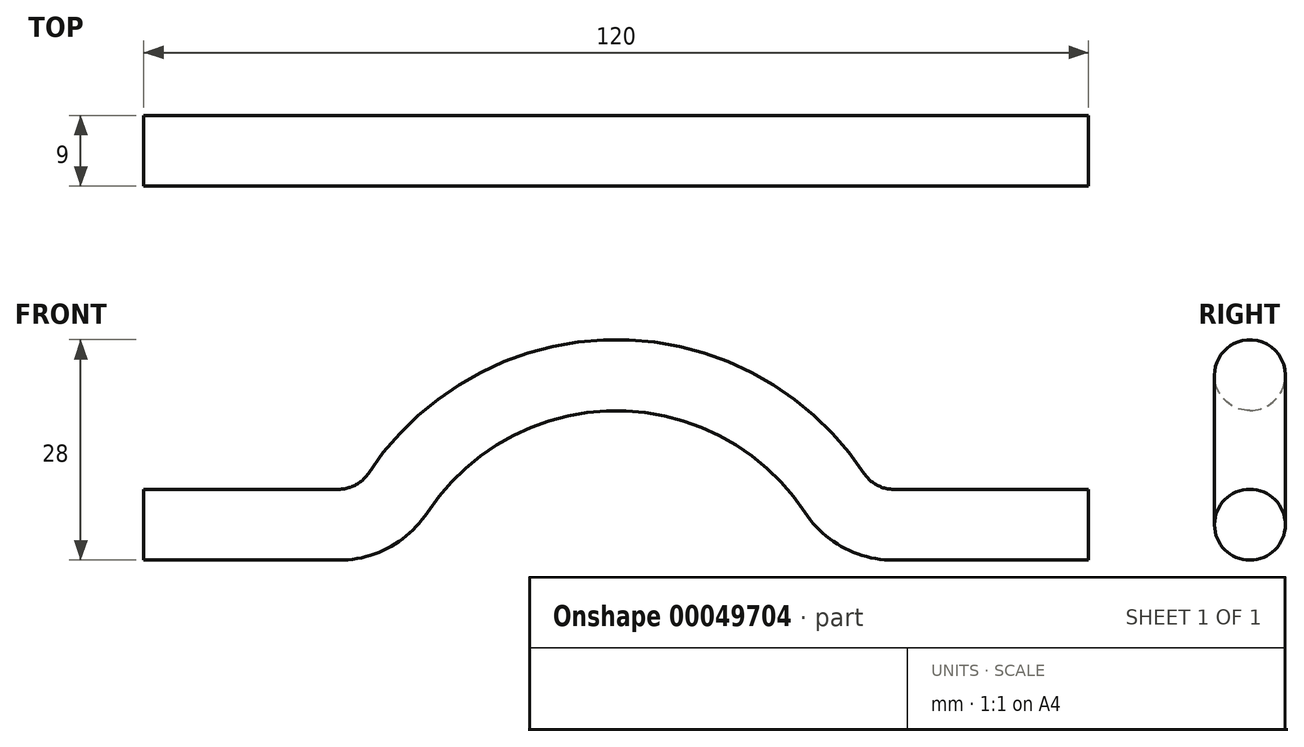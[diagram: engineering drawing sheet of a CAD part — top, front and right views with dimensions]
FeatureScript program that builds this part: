
annotation { "Feature Type Name" : "Feature", "Feature Type Description" : "" }
export const myFeature = defineFeature(function(context is Context, id is Id, definition is map)
    precondition{}
    {
        {
            var Q0;
            Q0=qCreatedBy(makeId("Front.planeOp"),FACE);
            var sketch = newSketch(context, id + "F0", { "sketchPlane" : qUnion([Q0])});
            skLineSegment(sketch, "E0", {"start": v(0, 0) * mm, "end": v(24.76, 0) * mm});
            skLineSegment(sketch, "E1", {"start": v(60, 23.82) * mm, "end": v(60, -14.96) * mm, "construction": true});
            skArc(sketch, "E2", {"start": v(60, 19) * mm, "mid": v(44.25, 15.03) * mm, "end": v(32.28, 4.05) * mm});
            skArc(sketch, "E3", {"start": v(87.72, 4.05) * mm, "mid": v(75.75, 15.03) * mm, "end": v(60, 19) * mm});
            skLineSegment(sketch, "E4", {"start": v(95.24, 0) * mm, "end": v(120, 0) * mm});
            skPoint(sketch, "E5.visualSharp", {"position": v(30, 0) * mm});
            skArc(sketch, "E5.filletArc", {"start": v(24.76, 0) * mm, "mid": v(29.03, 1.08) * mm, "end": v(32.28, 4.05) * mm});
            skPoint(sketch, "E6.visualSharp", {"position": v(90, 0) * mm});
            skArc(sketch, "E6.filletArc", {"start": v(87.72, 4.05) * mm, "mid": v(90.97, 1.08) * mm, "end": v(95.24, 0) * mm});
            skSolve(sketch);
        }
        {
            var Q0;
            Q0=qCreatedBy(makeId("Right.planeOp"),FACE);
            var sketch = newSketch(context, id + "F1", { "sketchPlane" : qUnion([Q0])});
            skPoint(sketch, "E7.0", {"position": v(0, 0) * mm});
            skCircle(sketch, "E8", {"center": v(0, 0) * mm, "radius": 4.5 * mm});
            skSolve(sketch);
        }
        {
            var Q0;
            Q0=makeQuery(id+"F1.imprint","IMPRINT",FACE,{"disambiguationData":[TD([[makeQuery(id+"F1.imprint","IMPRINT",EDGE,{"derivedFrom":sQuery(id+"F1.wireOp",EDGE,"E8")}),1.0]])]});
            var Q1;
            Q1=sQuery(id+"F0.wireOp",EDGE,"E0");
            var Q2;
            Q2=sQuery(id+"F0.wireOp",EDGE,"E5.filletArc");
            var Q3;
            Q3=sQuery(id+"F0.wireOp",EDGE,"E2");
            var Q4;
            Q4=sQuery(id+"F0.wireOp",EDGE,"E3");
            var Q5;
            Q5=sQuery(id+"F0.wireOp",EDGE,"E6.filletArc");
            var Q6;
            Q6=sQuery(id+"F0.wireOp",EDGE,"E4");
            sweep(context, id + "F2", {"profiles" : qUnion([Q0]), "path" : qUnion([Q1, Q2, Q3, Q4, Q5, Q6])});
        }
    });
